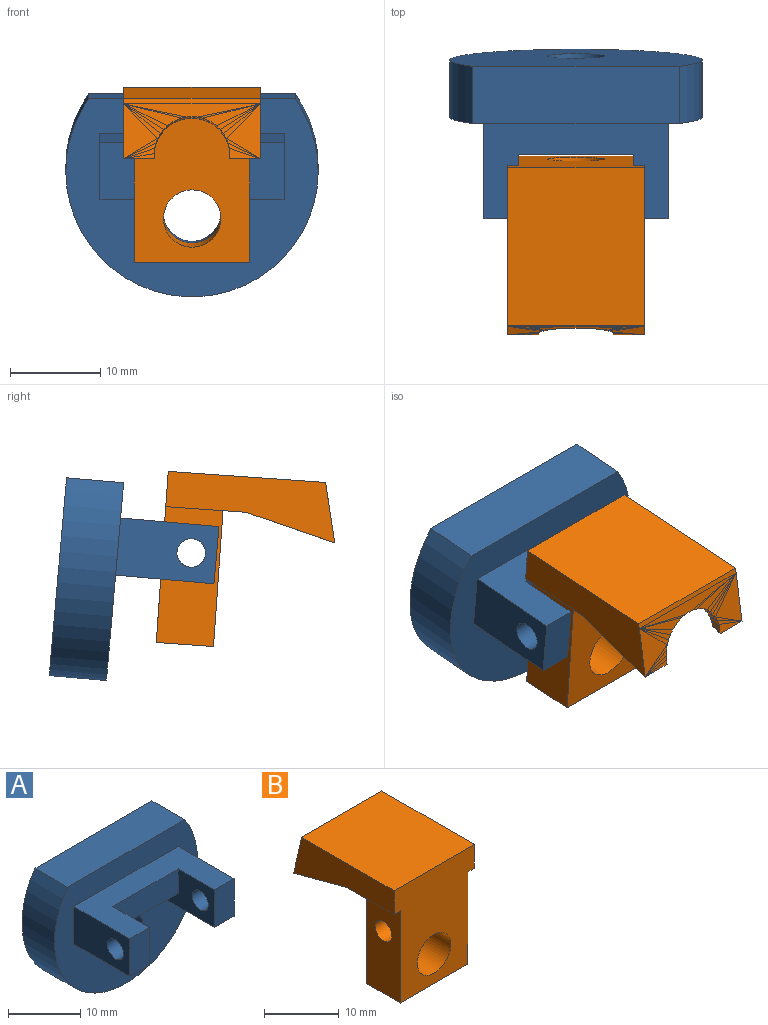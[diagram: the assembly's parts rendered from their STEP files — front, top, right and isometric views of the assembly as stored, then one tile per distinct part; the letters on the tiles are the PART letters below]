
ASSEMBLY  parts=2 mates=1
PART A: 18 faces, bbox 27.9x17.3x22 mm
  f0: plane 27.94x22mm, normal (0,-1,0), area 385.3mm2, adj f1,f2,f4,f5,f6,f7,f8,f10
  f1: plane 22.86x6.35mm, normal (0,0,1), area 145.2mm2, adj f0,f2,f3
  f2: cylinder r=13.97mm len=27.94mm, axis (0,1,0), area 387.4mm2, adj f0,f1,f3
  f3: plane 27.94x22mm, normal (0,1,0), area 486.2mm2, adj f1,f2,f4
  f4: cylinder r=3.17mm len=6.35mm, axis (0,-1,0), area 126.7mm2, adj f0,f3
  f5: plane 20.37x10.93mm, normal (0,0,1), area 131.9mm2, adj f0,f6,f8,f9,f10,f12,f13,f17
  f6: plane 10.93x6.35mm, normal (-1,0,0), area 45.8mm2, adj f0,f5,f7,f9,f15,f16,f17
  f7: plane 10.93x3.81mm, normal (0,0,-1), area 41.6mm2, adj f0,f6,f8,f9
  f8: plane 10.93x6.35mm, normal (1,0,0), area 61.5mm2, adj f0,f5,f7,f9,f15
  f9: plane 6.35x3.81mm, normal (0,-1,0), area 24.2mm2, adj f5,f6,f7,f8
  f10: plane 10.93x6.35mm, normal (-1,0,0), area 61.5mm2, adj f0,f5,f11,f13,f14
  f11: plane 10.93x3.81mm, normal (0,0,-1), area 41.6mm2, adj f0,f10,f12,f13
  f12: plane 10.93x6.35mm, normal (1,0,0), area 45.8mm2, adj f0,f5,f11,f13,f14,f16,f17
  f13: plane 6.35x3.81mm, normal (0,-1,0), area 24.2mm2, adj f5,f10,f11,f12
  f14: cylinder r=1.59mm len=3.81mm, axis (-1,0,0), area 38mm2, adj f10,f12
  f15: cylinder r=1.59mm len=3.81mm, axis (-1,0,0), area 38mm2, adj f6,f8
  f16: plane 12.75x3.81mm, normal (0,0,-1), area 48.6mm2, adj f0,f6,f12,f17
  f17: plane 12.75x4.13mm, normal (0,-1,0), area 52.6mm2, adj f5,f6,f12,f16
PART B: 109 faces, bbox 15.2x18.9x19 mm
  f0: plane 15.15x0.6mm, normal (0,0.97,0.22), area 9.3mm2, adj f1,f87,f97,f98
  f1: plane 18.94x6.6mm, normal (-1,0,0), area 82.6mm2, adj f0,f5,f93,f98,f99,f106
  f2: plane 7.46x4.32mm, normal (-1,0,0), area 20.9mm2, adj f3,f6,f25,f76,f100,f101,f107
  f3: plane 12.75x0.62mm, normal (0,-1,0), area 7.9mm2, adj f2,f4,f76,f100
  f4: plane 7.46x4.32mm, normal (1,0,0), area 20.9mm2, adj f3,f5,f25,f76,f99,f100,f107
  f5: plane 10.05x3.44mm, normal (0,-0.26,-0.97), area 17.3mm2, adj f1,f4,f7,f8,f25,f26,f73,f96
  f6: plane 10.05x3.44mm, normal (0,-0.26,-0.97), area 17.3mm2, adj f2,f24,f25,f71,f72,f74,f77,f97
  f7: plane 5.67x4.77mm, normal (1,0,0), area 17.3mm2, adj f5,f11,f25,f75
  f8: plane 1.75x0.57mm, normal (0,-0.97,-0.22), area 0.5mm2, adj f5,f9,f28
  f9: plane 1.88x1.13mm, normal (0,-0.97,-0.22), area 0.5mm2, adj f8,f10,f30
  f10: plane 2.1x1.67mm, normal (0,-0.97,-0.22), area 0.4mm2, adj f9,f11,f32
  f11: plane 5.67x2.38mm, normal (0,-0.97,-0.22), area 7.2mm2, adj f7,f10,f12,f34
  f12: plane 3.49x3.16mm, normal (0,-0.97,-0.22), area 2.4mm2, adj f11,f13,f36,f38
  f13: plane 3.64x2.63mm, normal (0,-0.97,-0.22), area 1.2mm2, adj f12,f14,f40
  f14: plane 4.16x2.29mm, normal (0,-0.97,-0.22), area 1.1mm2, adj f13,f15,f42
  f15: plane 4.71x2.02mm, normal (0,-0.97,-0.22), area 1mm2, adj f14,f16,f44
  f16: plane 5.29x1.82mm, normal (0,-0.97,-0.22), area 0.8mm2, adj f15,f17,f46
  f17: plane 11.75x1.7mm, normal (0,-0.97,-0.22), area 11.2mm2, adj f16,f18,f48,f49,f75
  f18: plane 5.29x1.82mm, normal (0,-0.97,-0.22), area 0.8mm2, adj f17,f19,f51
  f19: plane 4.71x2.02mm, normal (0,-0.97,-0.22), area 1mm2, adj f18,f20,f53
  f20: plane 4.16x2.29mm, normal (0,-0.97,-0.22), area 1.1mm2, adj f19,f21,f55
  f21: plane 3.64x2.63mm, normal (0,-0.97,-0.22), area 1.2mm2, adj f20,f22,f57
  f22: plane 5.67x3.16mm, normal (0,-0.97,-0.22), area 9.6mm2, adj f21,f23,f59,f61,f63,f74
  f23: plane 2.1x1.67mm, normal (0,-0.97,-0.22), area 0.4mm2, adj f22,f24,f65
  f24: plane 1.88x1.13mm, normal (0,-0.97,-0.22), area 1mm2, adj f6,f23,f67,f69
  f25: plane 12.75x4.32mm, normal (0,-0.97,-0.22), area 10.3mm2, adj f2,f4,f5,f6,f7,f74,f75,f76
  f26: plane 1.11x0.41mm, normal (1,0,0.02), area 0.2mm2, adj f5,f27,f73
  f27: plane 1.11x0.82mm, normal (1,0.02,-0.08), area 0.3mm2, adj f26,f28,f96
  f28: plane 1.11x0.82mm, normal (1,0.02,-0.08), area 0.3mm2, adj f8,f27,f29
  f29: plane 1.11x0.81mm, normal (0.98,0.05,-0.22), area 0.3mm2, adj f28,f30,f95
  f30: plane 1.12x0.81mm, normal (0.97,0.05,-0.22), area 0.3mm2, adj f9,f29,f31
  f31: plane 1.12x0.79mm, normal (0.93,0.08,-0.35), area 0.3mm2, adj f30,f32,f94
  f32: plane 1.12x0.79mm, normal (0.93,0.08,-0.35), area 0.3mm2, adj f10,f31,f33
  f33: plane 1.12x0.75mm, normal (0.87,0.11,-0.47), area 0.3mm2, adj f32,f34,f92
  f34: plane 1.12x0.75mm, normal (0.87,0.11,-0.48), area 0.3mm2, adj f11,f33,f35
  f35: plane 1.12x0.71mm, normal (0.8,0.14,-0.59), area 0.3mm2, adj f34,f36,f91
  f36: plane 1.13x0.71mm, normal (0.8,0.14,-0.59), area 0.3mm2, adj f12,f35,f37
  f37: plane 1.13x0.66mm, normal (0.7,0.16,-0.69), area 0.3mm2, adj f36,f38,f90
  f38: plane 1.13x0.66mm, normal (0.7,0.16,-0.69), area 0.3mm2, adj f12,f37,f39
  f39: plane 1.13x0.6mm, normal (0.6,0.18,-0.78), area 0.3mm2, adj f38,f40,f89
  f40: plane 1.13x0.6mm, normal (0.59,0.18,-0.78), area 0.3mm2, adj f13,f39,f41
  f41: plane 1.13x0.53mm, normal (0.48,0.2,-0.86), area 0.3mm2, adj f40,f42,f89
  f42: plane 1.13x0.53mm, normal (0.48,0.2,-0.86), area 0.3mm2, adj f14,f41,f43
  f43: plane 1.13x0.55mm, normal (0.35,0.21,-0.91), area 0.3mm2, adj f42,f44,f89
  f44: plane 1.13x0.55mm, normal (0.35,0.21,-0.91), area 0.3mm2, adj f15,f43,f45
  f45: plane 1.13x0.58mm, normal (0.21,0.22,-0.95), area 0.3mm2, adj f44,f46,f88
  f46: plane 1.13x0.58mm, normal (0.21,0.22,-0.95), area 0.3mm2, adj f16,f45,f47
  f47: plane 1.13x0.59mm, normal (0.07,0.22,-0.97), area 0.3mm2, adj f46,f48,f87
  f48: plane 1.13x0.59mm, normal (0.07,0.22,-0.97), area 0.3mm2, adj f17,f47,f49
  f49: plane 1.13x0.59mm, normal (-0.07,0.22,-0.97), area 0.3mm2, adj f17,f48,f50
  f50: plane 1.13x0.59mm, normal (-0.07,0.22,-0.97), area 0.3mm2, adj f49,f51,f87
  f51: plane 1.13x0.58mm, normal (-0.21,0.22,-0.95), area 0.3mm2, adj f18,f50,f52
  f52: plane 1.13x0.58mm, normal (-0.21,0.22,-0.95), area 0.3mm2, adj f51,f53,f86
  f53: plane 1.13x0.55mm, normal (-0.35,0.21,-0.91), area 0.3mm2, adj f19,f52,f54
  f54: plane 1.13x0.55mm, normal (-0.35,0.21,-0.91), area 0.3mm2, adj f53,f55,f85
  f55: plane 1.13x0.53mm, normal (-0.48,0.2,-0.86), area 0.3mm2, adj f20,f54,f56
  f56: plane 1.13x0.53mm, normal (-0.48,0.2,-0.86), area 0.3mm2, adj f55,f57,f85
  f57: plane 1.13x0.6mm, normal (-0.59,0.18,-0.78), area 0.3mm2, adj f21,f56,f58
  f58: plane 1.13x0.6mm, normal (-0.6,0.18,-0.78), area 0.3mm2, adj f57,f59,f85
  f59: plane 1.13x0.66mm, normal (-0.7,0.16,-0.69), area 0.3mm2, adj f22,f58,f60
  f60: plane 1.13x0.66mm, normal (-0.7,0.16,-0.69), area 0.3mm2, adj f59,f61,f84
  f61: plane 1.13x0.71mm, normal (-0.8,0.14,-0.59), area 0.3mm2, adj f22,f60,f62
  f62: plane 1.12x0.71mm, normal (-0.8,0.14,-0.59), area 0.3mm2, adj f61,f63,f83
  f63: plane 1.12x0.75mm, normal (-0.87,0.11,-0.48), area 0.3mm2, adj f22,f62,f64
  f64: plane 1.12x0.75mm, normal (-0.87,0.11,-0.47), area 0.3mm2, adj f63,f65,f82
  f65: plane 1.12x0.79mm, normal (-0.93,0.08,-0.35), area 0.3mm2, adj f23,f64,f66
  f66: plane 1.12x0.79mm, normal (-0.93,0.08,-0.35), area 0.3mm2, adj f65,f67,f80
  f67: plane 1.12x0.81mm, normal (-0.97,0.05,-0.22), area 0.3mm2, adj f24,f66,f68
  f68: plane 1.11x0.81mm, normal (-0.98,0.05,-0.22), area 0.3mm2, adj f67,f69,f79
  f69: plane 1.11x0.82mm, normal (-1,0.02,-0.08), area 0.3mm2, adj f24,f68,f70
  f70: plane 1.11x0.82mm, normal (-1,0.02,-0.08), area 0.3mm2, adj f69,f71,f78
  f71: plane 1.11x0.41mm, normal (-1,0,0.02), area 0.2mm2, adj f6,f70,f72
  f72: plane 0.62x0.58mm, normal (-1,-0.03,0.05), area 0.2mm2, adj f6,f71,f77
  f73: plane 0.62x0.58mm, normal (1,-0.03,0.05), area 0.2mm2, adj f5,f26,f96
  f74: plane 5.67x4.77mm, normal (-1,0,0), area 17.3mm2, adj f6,f22,f25,f75
  f75: plane 11.75x3.46mm, normal (0,0.22,-0.97), area 41.7mm2, adj f7,f17,f25,f74
  f76: plane 12.75x3.93mm, normal (0,0.22,-0.97), area 51.4mm2, adj f2,f3,f4,f25
  f77: plane 3.44x0.58mm, normal (0,0.98,0.22), area 1mm2, adj f6,f72,f78
  f78: plane 3.45x1.15mm, normal (0,0.98,0.22), area 1mm2, adj f70,f77,f79
  f79: plane 3.58x1.71mm, normal (0,0.98,0.22), area 0.9mm2, adj f68,f78,f80
  f80: plane 3.79x2.25mm, normal (0,0.98,0.22), area 0.8mm2, adj f66,f79,f81
  f81: plane 6x3.79mm, normal (0,0.98,0.22), area 11.7mm2, adj f80,f82,f97
  f82: plane 4.08x3.75mm, normal (0,0.98,0.22), area 1.5mm2, adj f64,f81,f83
  f83: plane 4.44x3.24mm, normal (0,0.98,0.22), area 1.6mm2, adj f62,f82,f84
  f84: plane 4.86x2.78mm, normal (0,0.98,0.22), area 1.5mm2, adj f60,f83,f85
  f85: plane 6.41x2.38mm, normal (0,0.98,0.22), area 3.8mm2, adj f54,f56,f58,f84,f86
  f86: plane 6.99x1.56mm, normal (0,0.98,0.22), area 0.9mm2, adj f52,f85,f87
  f87: plane 15.15x1.44mm, normal (0,0.98,0.22), area 12mm2, adj f0,f47,f50,f86,f88
  f88: plane 6.99x1.56mm, normal (0,0.98,0.22), area 0.9mm2, adj f45,f87,f89
  f89: plane 6.41x2.38mm, normal (0,0.98,0.22), area 3.8mm2, adj f39,f41,f43,f88,f90
  f90: plane 4.86x2.78mm, normal (0,0.98,0.22), area 1.5mm2, adj f37,f89,f91
  f91: plane 4.44x3.24mm, normal (0,0.98,0.22), area 1.6mm2, adj f35,f90,f92
  f92: plane 4.08x3.75mm, normal (0,0.98,0.22), area 1.5mm2, adj f33,f91,f93
  f93: plane 6x3.79mm, normal (0,0.98,0.22), area 11.7mm2, adj f1,f92,f94
  f94: plane 3.79x2.25mm, normal (0,0.98,0.22), area 0.8mm2, adj f31,f93,f95
  f95: plane 3.58x1.71mm, normal (0,0.98,0.22), area 0.9mm2, adj f29,f94,f96
  f96: plane 3.45x1.15mm, normal (0,0.98,0.22), area 2mm2, adj f5,f27,f73,f95
  f97: plane 18.94x6.6mm, normal (1,0,0), area 82.6mm2, adj f0,f6,f81,f98,f101,f106
  f98: plane 17.45x15.15mm, normal (0,0,1), area 264.4mm2, adj f0,f1,f97,f106
  f99: plane 8.89x1.2mm, normal (0,0,-1), area 10.7mm2, adj f1,f4,f5,f102,f106
  f100: plane 12.75x2.54mm, normal (0,0,-1), area 32.4mm2, adj f2,f3,f4,f107
  f101: plane 8.89x1.2mm, normal (0,0,-1), area 10.7mm2, adj f2,f6,f97,f104,f106
  f102: plane 15.07x6.35mm, normal (-1,0,0), area 87.8mm2, adj f99,f103,f106,f107,f108
  f103: plane 12.75x6.35mm, normal (0,0,-1), area 81mm2, adj f102,f104,f106,f107
  f104: plane 15.07x6.35mm, normal (1,0,0), area 87.8mm2, adj f101,f103,f106,f107,f108
  f105: cylinder r=3.17mm len=6.35mm, axis (0,1,0), area 126.7mm2, adj f106,f107
  f106: plane 18.98x15.15mm, normal (0,-1,0), area 219.7mm2, adj f1,f97,f98,f99,f101,f102,f103,f104
  f107: plane 17.78x12.75mm, normal (0,1,0), area 195mm2, adj f2,f4,f100,f102,f103,f104,f105
  f108: cylinder r=1.59mm len=12.75mm, axis (1,0,0), area 127.2mm2, adj f102,f104
PLACE A rot(axis=(1,0,0),5deg) t=(6.58,-23.43,2.13)mm fixed
PLACE B rot(axis=(0,-0.03,1),180deg) t=(6.58,-19.33,-2.18)mm
MATE revolute B.f108 <-> A.f14  axis (1,0,0) through (12.96,-37.94,1.81)mm
